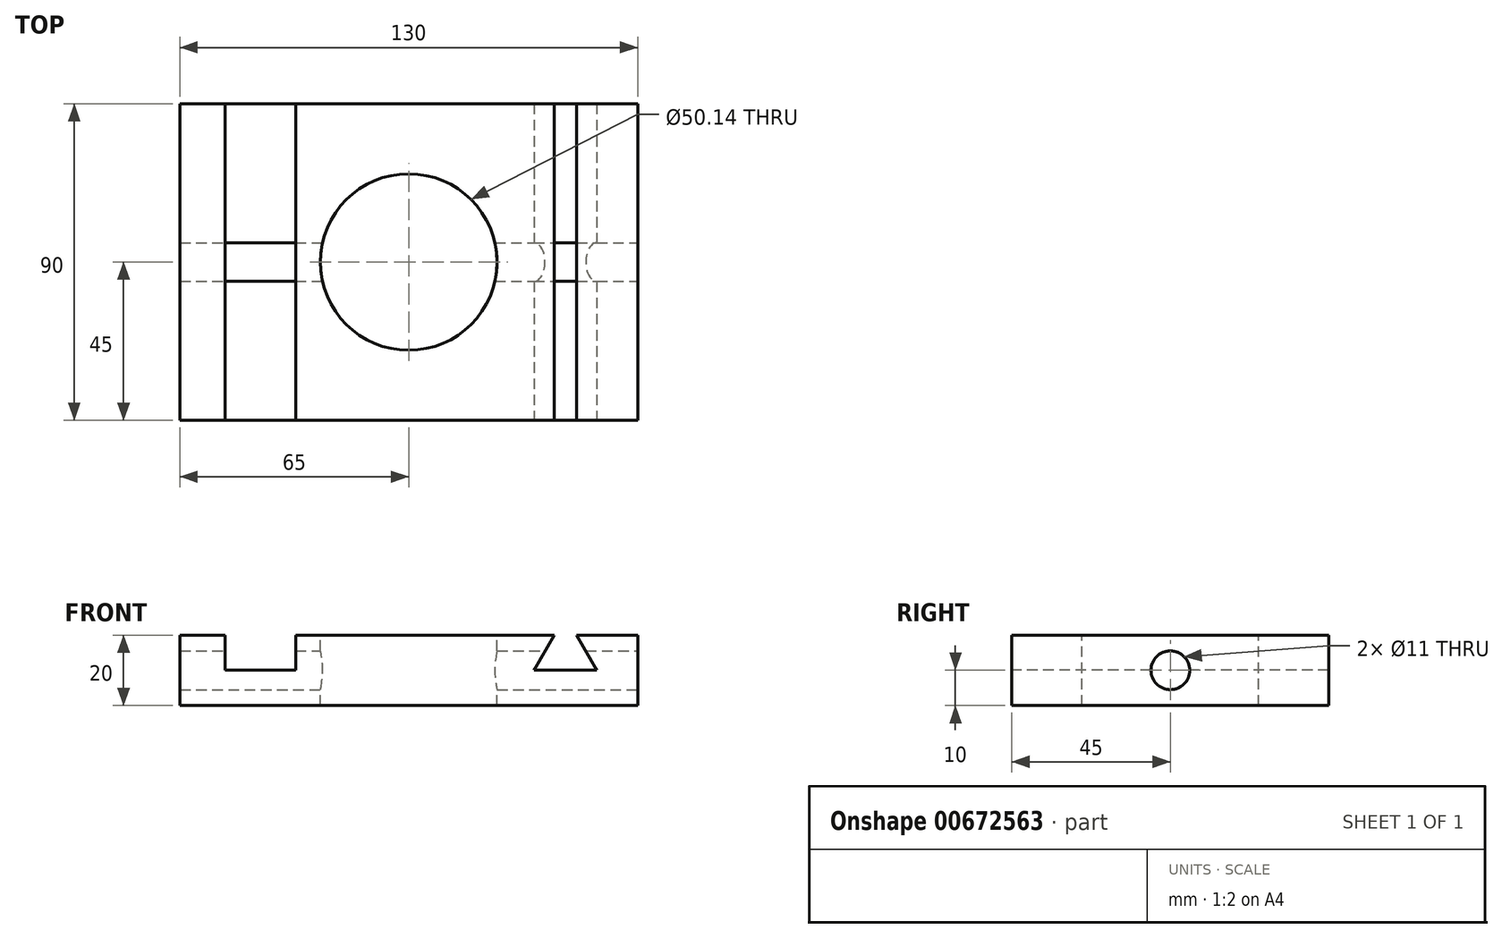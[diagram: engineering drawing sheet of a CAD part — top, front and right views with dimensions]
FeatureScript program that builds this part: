
annotation { "Feature Type Name" : "Feature", "Feature Type Description" : "" }
export const myFeature = defineFeature(function(context is Context, id is Id, definition is map)
    precondition{}
    {
        {
            var Q0;
            Q0=qCreatedBy(makeId("Top.planeOp"),FACE);
            var sketch = newSketch(context, id + "F0", { "sketchPlane" : qUnion([Q0])});
            skLineSegment(sketch, "E0.bottom", {"start": v(65, -45) * mm, "end": v(-65, -45) * mm});
            skLineSegment(sketch, "E0.top", {"start": v(65, 45) * mm, "end": v(-65, 45) * mm});
            skLineSegment(sketch, "E0.left", {"start": v(65, -45) * mm, "end": v(65, 45) * mm});
            skLineSegment(sketch, "E0.right", {"start": v(-65, -45) * mm, "end": v(-65, 45) * mm});
            skPoint(sketch, "E0.middle", {"position": v(0, 0) * mm});
            skSolve(sketch);
        }
        {
            var Q0;
            Q0=makeQuery(id+"F0.imprint","IMPRINT",FACE,{"disambiguationData":[TD([[makeQuery(id+"F0.imprint","IMPRINT",EDGE,{"derivedFrom":sQuery(id+"F0.wireOp",EDGE,"E0.bottom")}),-1.0]])]});
            extrude(context, id + "F1", {"entities" : qUnion([Q0]), "depth" : 20 * mm, "offsetDistance" : 25.4 * mm});
        }
        {
            var Q0;
            Q0=makeQuery(id+"F1.opExtrude","CAP_FACE",FACE,{"disambiguationData":[OSD([sQuery(id+"F0.wireOp",EDGE,"E0.bottom"),sQuery(id+"F0.wireOp",EDGE,"E0.top"),sQuery(id+"F0.wireOp",EDGE,"E0.left"),sQuery(id+"F0.wireOp",EDGE,"E0.right")])],"isStart":false});
            var sketch = newSketch(context, id + "F2", { "sketchPlane" : qUnion([Q0])});
            skLineSegment(sketch, "E1.bottom", {"start": v(-52.15, 45) * mm, "end": v(-32.15, 45) * mm});
            skLineSegment(sketch, "E1.top", {"start": v(-52.15, -45) * mm, "end": v(-32.15, -45) * mm});
            skLineSegment(sketch, "E1.left", {"start": v(-52.15, 45) * mm, "end": v(-52.15, -45) * mm});
            skLineSegment(sketch, "E1.right", {"start": v(-32.15, 45) * mm, "end": v(-32.15, -45) * mm});
            skSolve(sketch);
        }
        {
            var Q0;
            Q0=makeQuery(id+"F2.imprint","IMPRINT",FACE,{"disambiguationData":[TD([[makeQuery(id+"F2.imprint","IMPRINT",EDGE,{"derivedFrom":sQuery(id+"F2.wireOp",EDGE,"E1.bottom")}),1.0]])]});
            extrude(context, id + "F3", {"entities" : qUnion([Q0]), "operationType" : NewBodyOperationType.REMOVE, "oppositeDirection" : true, "depth" : 10 * mm, "offsetDistance" : 25 * mm});
        }
        {
            var Q0;
            {var subQ0=sQuery(id+"F0.wireOp",EDGE,"E0.bottom");var subQ1=sQuery(id+"F0.wireOp",EDGE,"E0.top");var subQ2=sQuery(id+"F0.wireOp",EDGE,"E0.left");Q0=makeQuery(id+"F3.boolean.opBoolean","SPLIT",FACE,{"disambiguationData":[TD([makeQuery(id+"F1.opExtrude","SWEPT_FACE",FACE,{"disambiguationData":[OSD([subQ2])]})])],"derivedFrom":makeQuery(id+"F1.opExtrude","CAP_FACE",FACE,{"disambiguationData":[OSD([subQ0,subQ1,subQ2,sQuery(id+"F0.wireOp",EDGE,"E0.right")])],"isStart":false})});}
            var sketch = newSketch(context, id + "F4", { "sketchPlane" : qUnion([Q0])});
            skCircle(sketch, "E2", {"center": v(0, 0) * mm, "radius": 25.07 * mm});
            skSolve(sketch);
        }
        {
            var Q0;
            Q0=makeQuery(id+"F4.imprint","IMPRINT",FACE,{"disambiguationData":[TD([[makeQuery(id+"F4.imprint","IMPRINT",EDGE,{"derivedFrom":sQuery(id+"F4.wireOp",EDGE,"E2")}),1.0]])]});
            extrude(context, id + "F5", {"entities" : qUnion([Q0]), "operationType" : NewBodyOperationType.REMOVE, "endBound" : BoundingType.THROUGH_ALL, "oppositeDirection" : true, "depth" : 25 * mm, "offsetDistance" : 25 * mm});
        }
        {
            var Q0;
            Q0=makeQuery(id+"F1.opExtrude","SWEPT_FACE",FACE,{"disambiguationData":[OSD([sQuery(id+"F0.wireOp",EDGE,"E0.left")])]});
            var sketch = newSketch(context, id + "F6", { "sketchPlane" : qUnion([Q0])});
            skCircle(sketch, "E3", {"center": v(0, 10) * mm, "radius": 5.5 * mm});
            skPoint(sketch, "E3.centerSnap0", {"position": v(45, 10) * mm});
            skSolve(sketch);
        }
        {
            var Q0;
            Q0=makeQuery(id+"F6.imprint","IMPRINT",FACE,{"disambiguationData":[TD([[makeQuery(id+"F6.imprint","IMPRINT",EDGE,{"derivedFrom":sQuery(id+"F6.wireOp",EDGE,"E3")}),1.0]])]});
            extrude(context, id + "F7", {"entities" : qUnion([Q0]), "operationType" : NewBodyOperationType.REMOVE, "endBound" : BoundingType.THROUGH_ALL, "oppositeDirection" : true, "depth" : 25 * mm, "offsetDistance" : 25 * mm});
        }
        {
            var Q0;
            Q0=makeQuery(id+"F1.opExtrude","SWEPT_FACE",FACE,{"disambiguationData":[OSD([sQuery(id+"F0.wireOp",EDGE,"E0.bottom")])]});
            var sketch = newSketch(context, id + "F8", { "sketchPlane" : qUnion([Q0])});
            skLineSegment(sketch, "E4", {"start": v(41.32, 20) * mm, "end": v(35.55, 10) * mm});
            skLineSegment(sketch, "E5", {"start": v(35.55, 10) * mm, "end": v(53.44, 10) * mm});
            skLineSegment(sketch, "E6", {"start": v(53.44, 10) * mm, "end": v(47.66, 20) * mm});
            skLineSegment(sketch, "E7", {"start": v(47.66, 20) * mm, "end": v(41.32, 20) * mm});
            skSolve(sketch);
        }
        {
            var Q0;
            Q0=makeQuery(id+"F8.imprint","IMPRINT",FACE,{"disambiguationData":[TD([[makeQuery(id+"F8.imprint","IMPRINT",EDGE,{"derivedFrom":sQuery(id+"F8.wireOp",EDGE,"E4")}),1.0]])]});
            extrude(context, id + "F9", {"entities" : qUnion([Q0]), "operationType" : NewBodyOperationType.REMOVE, "endBound" : BoundingType.THROUGH_ALL, "oppositeDirection" : true, "depth" : 25 * mm, "offsetDistance" : 25 * mm});
        }
    });
